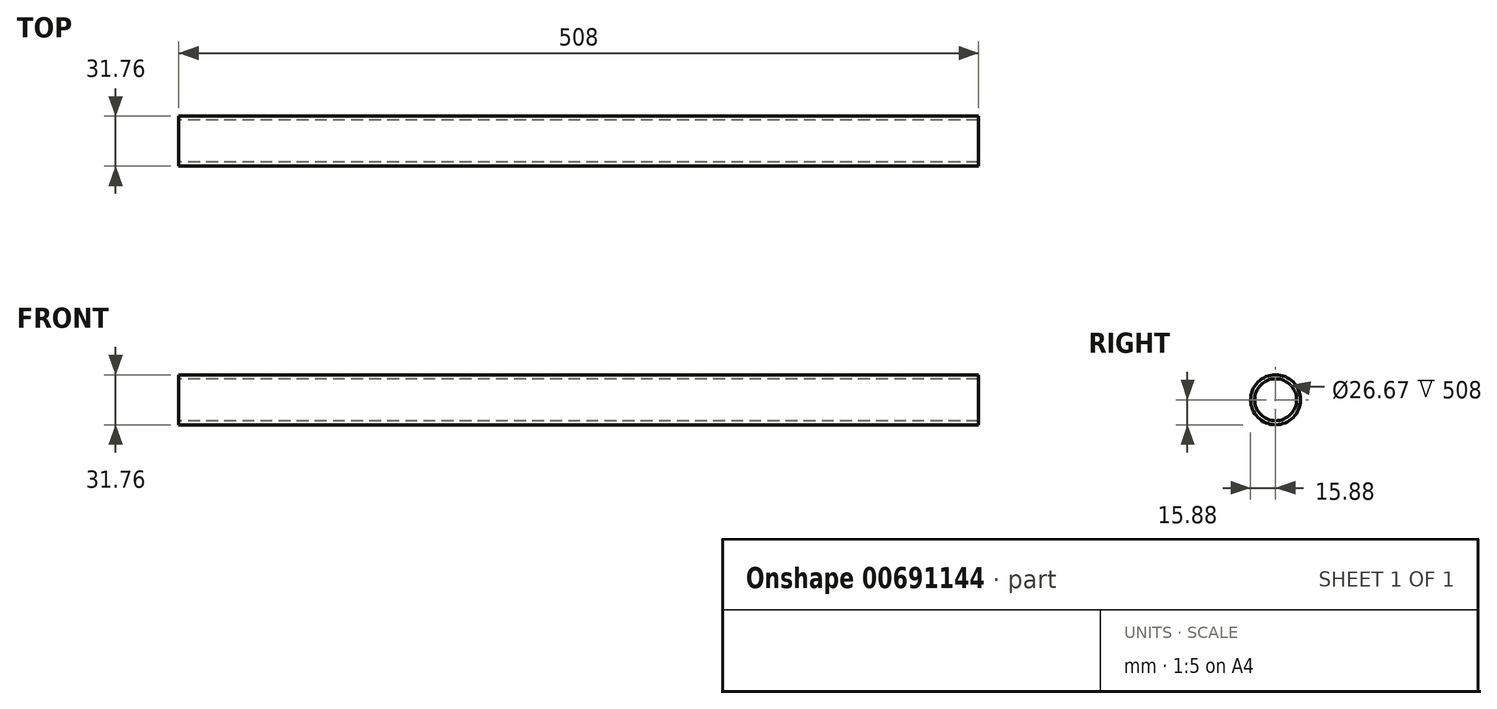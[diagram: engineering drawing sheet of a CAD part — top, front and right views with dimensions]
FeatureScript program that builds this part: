
annotation { "Feature Type Name" : "Feature", "Feature Type Description" : "" }
export const myFeature = defineFeature(function(context is Context, id is Id, definition is map)
    precondition{}
    {
        {
            var Q0;
            Q0=qCreatedBy(makeId("Right.planeOp"),FACE);
            var sketch = newSketch(context, id + "F0", { "sketchPlane" : qUnion([Q0])});
            skCircle(sketch, "E0", {"center": v(0, 0) * mm, "radius": 15.88 * mm});
            skSolve(sketch);
        }
        {
            var Q0;
            Q0=makeQuery(id+"F0.imprint","IMPRINT",FACE,{"disambiguationData":[TD([[makeQuery(id+"F0.imprint","IMPRINT",EDGE,{"derivedFrom":sQuery(id+"F0.wireOp",EDGE,"E0")}),1.0]])]});
            extrude(context, id + "F1", {"entities" : qUnion([Q0]), "endBound" : BoundingType.SYMMETRIC, "depth" : 508 * mm, "offsetDistance" : 25.4 * mm});
        }
        {
            var Q0;
            Q0=makeQuery(id+"F1.opExtrude","CAP_FACE",FACE,{"disambiguationData":[OSD([sQuery(id+"F0.wireOp",EDGE,"E0")])],"isStart":false});
            var Q1;
            Q1=makeQuery(id+"F1.opExtrude","CAP_FACE",FACE,{"disambiguationData":[OSD([sQuery(id+"F0.wireOp",EDGE,"E0")])],"isStart":true});
            shell(context, id + "F2", {"entities" : qUnion([Q0, Q1]), "thickness" : 2.54 * mm});
        }
    });
